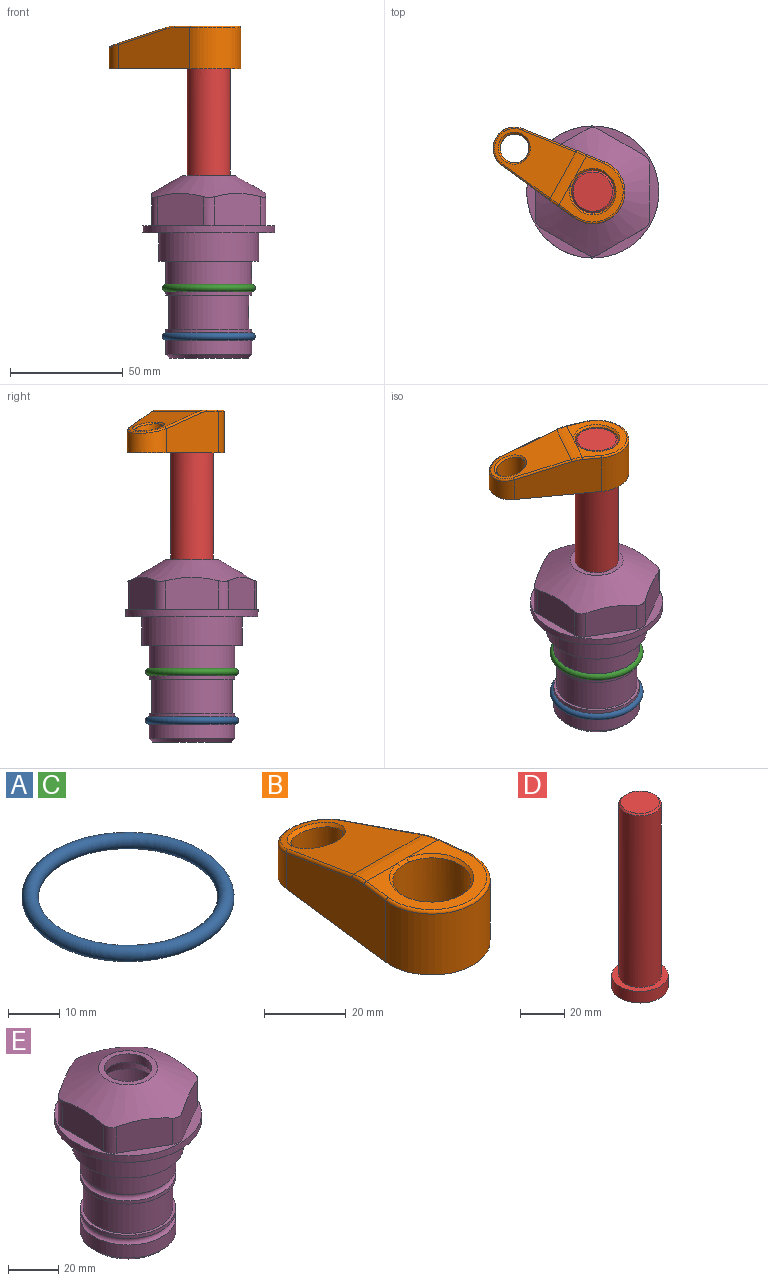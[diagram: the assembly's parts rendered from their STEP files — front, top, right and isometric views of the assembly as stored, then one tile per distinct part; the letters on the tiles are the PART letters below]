
ASSEMBLY  parts=5 mates=4
PART A: 1 faces, bbox 44.7x44.7x3.2 mm
  f0: torus R=19.05mm, axis (0,0,1), area 1193.9mm2
PART B: 31 faces, bbox 31.7x65.5x19.8 mm
  f0: plane 39.12x18.26mm, normal (0.99,0.12,0), area 612.2mm2, adj f1,f4,f7,f11,f13,f15
  f1: cylinder r=9.53mm len=18.91mm, axis (0,0,-1), area 296.1mm2, adj f0,f2,f7,f17
  f2: plane 39.12x18.26mm, normal (-0.99,0.12,0), area 612.2mm2, adj f1,f4,f7,f12,f14,f16
  f3: cylinder r=6.35mm len=12.7mm, axis (0,0,-1), area 362.4mm2, adj f7,f18
  f4: cylinder r=14.29mm len=28.58mm, axis (0,0,-1), area 882.2mm2, adj f0,f2,f7,f10
  f5: cylinder r=9.53mm len=19.05mm, axis (0,0,-1), area 1092.6mm2, adj f7,f19,f20
  f6: plane 26.99x23.69mm, normal (0,0,1), area 216.2mm2, adj f9,f10,f11,f12,f19
  f7: plane 63.5x28.58mm, normal (0,0,-1), area 661.8mm2, adj f0,f1,f2,f3,f4,f5,f22,f23
  f8: plane 33.52x23.6mm, normal (0,0.26,0.97), area 486mm2, adj f9,f15,f16,f17,f18
  f9: cylinder r=19.05mm len=24.72mm, axis (1,0,0), area 120.4mm2, adj f6,f8,f13,f14,f20
  f10: torus R=13.49mm, axis (0,0,1), area 59mm2, adj f4,f6,f11,f12
  f11: cylinder r=0.79mm len=8.67mm, axis (0.12,-0.99,0), area 10.8mm2, adj f0,f6,f10,f13
  f12: cylinder r=0.79mm len=8.67mm, axis (0.12,0.99,0), area 10.8mm2, adj f2,f6,f10,f14
  f13: bspline ~4.95x1.42mm, area 6.1mm2, adj f0,f9,f11,f15
  f14: bspline ~4.95x1.42mm, area 6.1mm2, adj f2,f9,f12,f16
  f15: cylinder r=0.79mm len=25.95mm, axis (0.12,-0.96,0.26), area 32.9mm2, adj f0,f8,f13,f17
  f16: cylinder r=0.79mm len=25.95mm, axis (0.12,0.96,-0.26), area 32.9mm2, adj f2,f8,f14,f17
  f17: bspline ~18.91x8.38mm, area 30mm2, adj f1,f8,f15,f16
  f18: bspline ~14.29x14.29mm, area 48.3mm2, adj f3,f8
  f19: cone r=9.53mm half-angle=45deg, axis (0,0,1), area 66.5mm2, adj f5,f6,f20
  f20: bspline ~3.22x0.96mm, area 3.5mm2, adj f5,f9,f19
  f21: plane 2.75x2.72mm, normal (0,0,-1), area 2.9mm2, adj f23,f25,f28
  f22: plane 23.05x15.88mm, normal (-0.99,-0.12,0), area 323.6mm2, adj f7,f25,f26,f27,f28,f29
  f23: plane 23.05x15.88mm, normal (0.99,-0.12,0), area 323.6mm2, adj f7,f21,f25,f27,f28,f30
  f24: cylinder r=9.53mm len=10.69mm, axis (0,0,-1), area 114.7mm2, adj f7,f27,f29,f30
  f25: cylinder r=12.7mm len=20.59mm, axis (0,0,-1), area 381.1mm2, adj f7,f21,f22,f23,f26,f28
  f26: plane 2.75x2.72mm, normal (0,0,-1), area 2.9mm2, adj f22,f25,f28
  f27: plane 19.72x18.37mm, normal (0,-0.26,-0.97), area 291.8mm2, adj f22,f23,f24,f28,f29,f30
  f28: cylinder r=15.88mm len=19.92mm, axis (1,0,0), area 54.8mm2, adj f21,f22,f23,f25,f26,f27
  f29: cylinder r=1.59mm len=11mm, axis (0,0,-1), area 34.7mm2, adj f7,f22,f24,f27
  f30: cylinder r=1.59mm len=11mm, axis (0,0,-1), area 34.7mm2, adj f7,f23,f24,f27
PART C: same geometry as A
PART D: 6 faces, bbox 25.4x25.4x101.6 mm
  f0: plane 17.46x17.46mm, normal (0,0,1), area 239.5mm2, adj f5
  f1: plane 25.4x25.4mm, normal (0,0,-1), area 506.7mm2, adj f2
  f2: cylinder r=12.7mm len=25.4mm, axis (0,0,1), area 506.7mm2, adj f1,f3
  f3: plane 25.4x25.4mm, normal (0,0,1), area 221.7mm2, adj f2,f4
  f4: cylinder r=9.53mm len=94.46mm, axis (0,0,1), area 5653mm2, adj f3,f5
  f5: cone r=8.73mm half-angle=45deg, axis (0,0,-1), area 64.4mm2, adj f0,f4
PART E: 36 faces, bbox 58.7x58.7x81 mm
  f0: cylinder r=17.78mm len=35.56mm, axis (0,0,1), area 1670.8mm2, adj f23,f24,f31
  f1: cylinder r=19.05mm len=38.1mm, axis (0,0,1), area 1191.9mm2, adj f26,f27,f30
  f2: plane 58.66x58.66mm, normal (0,0,-1), area 1150.6mm2, adj f3,f28
  f3: cylinder r=29.33mm len=58.66mm, axis (0,0,-1), area 585.1mm2, adj f2,f4
  f4: plane 58.66x58.66mm, normal (0,0,1), area 475.9mm2, adj f3,f5,f6,f7,f8,f9,f10,f11
  f5: plane 20.32x14.34mm, normal (-0.5,0.87,0), area 324.4mm2, adj f4,f15,f16,f17
  f6: plane 20.32x14.34mm, normal (0.5,0.87,0), area 324.4mm2, adj f4,f14,f15,f17
  f7: plane 23.48x14.34mm, normal (1,0,0), area 324.4mm2, adj f4,f13,f14,f17
  f8: plane 20.32x14.34mm, normal (0.5,-0.87,0), area 324.4mm2, adj f4,f12,f13,f17
  f9: plane 20.32x14.34mm, normal (-0.5,-0.87,0), area 324.4mm2, adj f4,f11,f12,f17
  f10: plane 23.48x14.34mm, normal (-1,0,0), area 324.4mm2, adj f4,f11,f16,f17
  f11: cylinder r=5.08mm len=12.85mm, axis (0,0,-1), area 67.2mm2, adj f4,f9,f10,f17
  f12: cylinder r=5.08mm len=12.85mm, axis (0,0,-1), area 67.2mm2, adj f4,f8,f9,f17
  f13: cylinder r=5.08mm len=12.85mm, axis (0,0,-1), area 67.2mm2, adj f4,f7,f8,f17
  f14: cylinder r=5.08mm len=12.85mm, axis (0,0,-1), area 67.2mm2, adj f4,f6,f7,f17
  f15: cylinder r=5.08mm len=12.85mm, axis (0,0,-1), area 67.2mm2, adj f4,f5,f6,f17
  f16: cylinder r=5.08mm len=12.85mm, axis (0,0,-1), area 67.2mm2, adj f4,f5,f10,f17
  f17: cone r=11.73mm half-angle=60deg, axis (0,0,-1), area 2071.8mm2, adj f5,f6,f7,f8,f9,f10,f11,f12
  f18: plane 23.46x23.46mm, normal (0,0,1), area 147.4mm2, adj f17,f35
  f19: plane 34.93x34.93mm, normal (0,0,-1), area 958mm2, adj f29
  f20: cylinder r=19.05mm len=38.1mm, axis (0,0,1), area 760.1mm2, adj f21,f29
  f21: torus R=19.05mm, axis (0,0,1), area 565.3mm2, adj f20,f22
  f22: cylinder r=19.05mm len=38.1mm, axis (0,0,1), area 190mm2, adj f21,f23
  f23: plane 38.1x38.1mm, normal (0,0,1), area 146.9mm2, adj f0,f22
  f24: plane 38.1x38.1mm, normal (0,0,-1), area 146.9mm2, adj f0,f25
  f25: cylinder r=19.05mm len=38.1mm, axis (0,0,1), area 190mm2, adj f24,f26
  f26: torus R=19.05mm, axis (0,0,1), area 565.3mm2, adj f1,f25
  f27: plane 44.45x44.45mm, normal (0,0,-1), area 411.7mm2, adj f1,f28
  f28: cylinder r=22.23mm len=44.45mm, axis (0,0,1), area 1773.5mm2, adj f2,f27
  f29: cone r=19.05mm half-angle=45deg, axis (0,0,1), area 257.5mm2, adj f19,f20
  f30: cylinder r=3.17mm len=6.75mm, axis (-1,0,0), area 128mm2, adj f1,f33
  f31: cylinder r=3.17mm len=6.35mm, axis (-1,0,0), area 102.5mm2, adj f0,f33
  f32: plane 25.4x25.4mm, normal (0,0,1), area 506.7mm2, adj f33
  f33: cylinder r=12.7mm len=66.42mm, axis (0,0,-1), area 5236.2mm2, adj f30,f31,f32,f34
  f34: cone r=9.53mm half-angle=30deg, axis (0,0,-1), area 443.4mm2, adj f33,f35
  f35: cylinder r=9.53mm len=19.05mm, axis (0,0,-1), area 240.9mm2, adj f18,f34
PLACE A t=(0,0,-21.59)mm
PLACE B rot(axis=(0,0,1),61.1deg) t=(0,0,28.35)mm
PLACE C at identity
PLACE D rot(axis=(0,0,1),61.1deg) t=(0,0,27.55)mm
PLACE E at identity fixed
MATE cylindrical D.f2 <-> E.f0  axis (0,0,-1) through (0,0,-10.55)mm
MATE fastened A.f0 <-> E.f0  axis (0,0,1) through (0,0,-46.1)mm
MATE fastened D.f2 <-> B.f4  axis (0,0,1) through (0,0,91.05)mm
MATE fastened C.f0 <-> E.f0  axis (0,0,1) through (0,0,-24.51)mm
